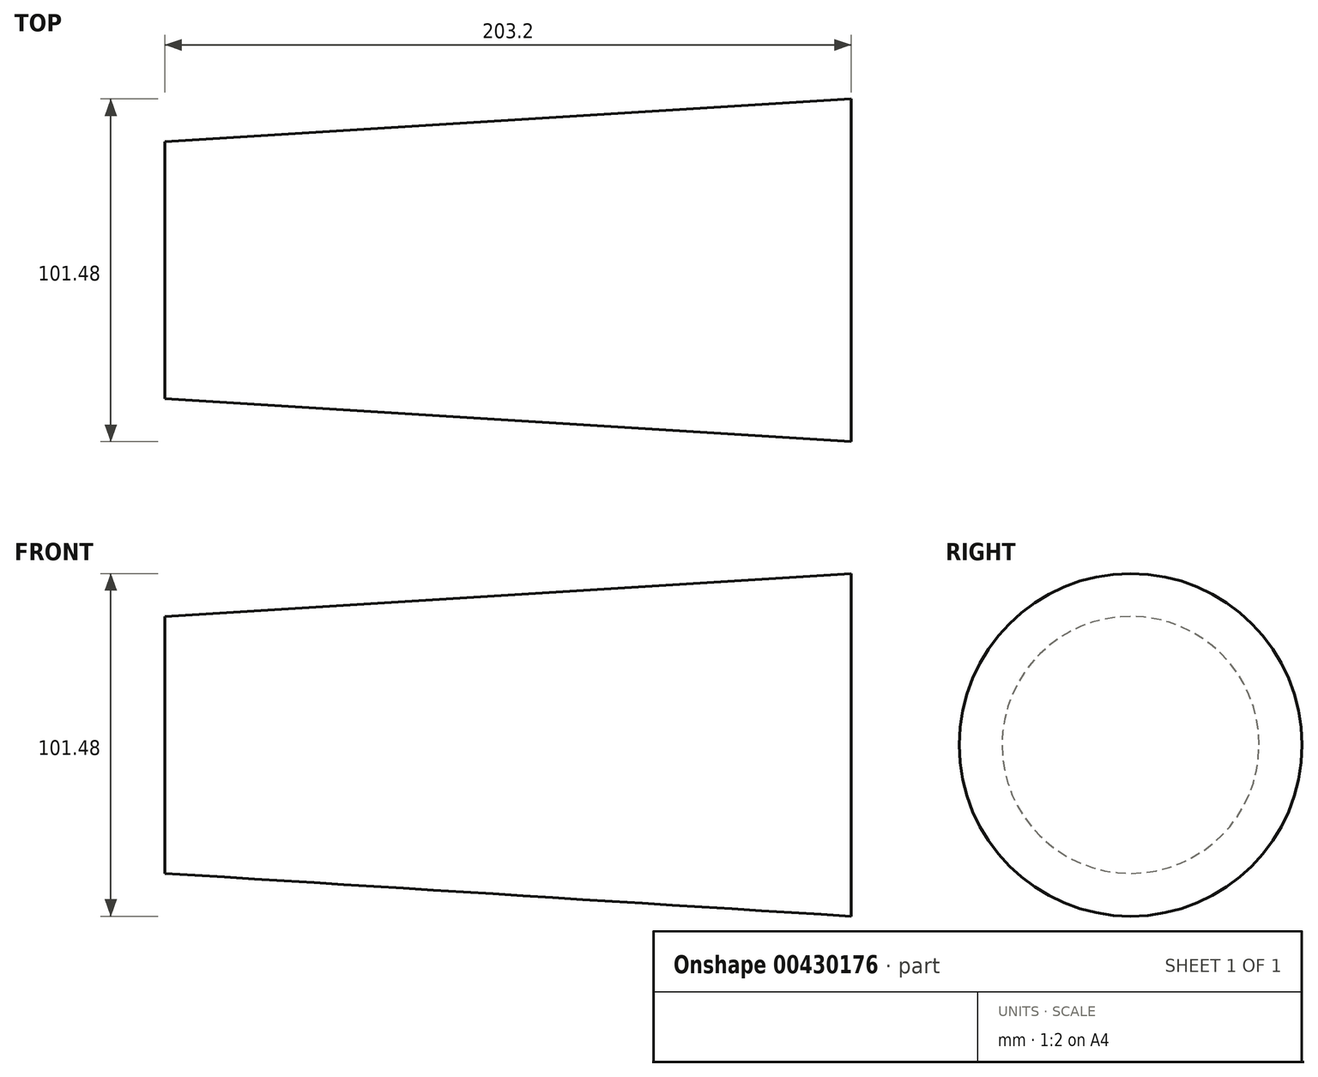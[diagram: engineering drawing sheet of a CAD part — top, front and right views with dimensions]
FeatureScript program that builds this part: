
annotation { "Feature Type Name" : "Feature", "Feature Type Description" : "" }
export const myFeature = defineFeature(function(context is Context, id is Id, definition is map)
    precondition{}
    {
        {
            var Q0;
            Q0=qCreatedBy(makeId("Front.planeOp"),FACE);
            var sketch = newSketch(context, id + "F0", { "sketchPlane" : qUnion([Q0])});
            skLineSegment(sketch, "E0", {"start": v(0, 0) * mm, "end": v(811.89, 0) * mm});
            skLineSegment(sketch, "E1", {"start": v(811.89, 0) * mm, "end": v(0, 0) * mm, "construction": true});
            skLineSegment(sketch, "E2", {"start": v(811.89, 50.74) * mm, "end": v(0, 0) * mm});
            skLineSegment(sketch, "E3", {"start": v(811.89, 50.74) * mm, "end": v(811.89, 0) * mm});
            skLineSegment(sketch, "E4", {"start": v(608.69, 38.04) * mm, "end": v(608.69, 0) * mm});
            skSolve(sketch);
        }
        {
            var Q0;
            {var subQ0=sQuery(id+"F0.wireOp",EDGE,"E3");Q0=makeQuery(id+"F0.imprint","IMPRINT",FACE,{"disambiguationData":[TD([[makeQuery(id+"F0.imprint","IMPRINT",EDGE,{"derivedFrom":subQ0}),-1.0]])]});}
            var Q1;
            Q1=sQuery(id+"F0.wireOp",EDGE,"E1");
            revolve(context, id + "F1", {"surfaceOperationType" : NewSurfaceOperationType.NEW, "entities" : qUnion([Q0]), "axis" : qUnion([Q1]), "revolveType" : RevolveType.FULL});
        }
    });
